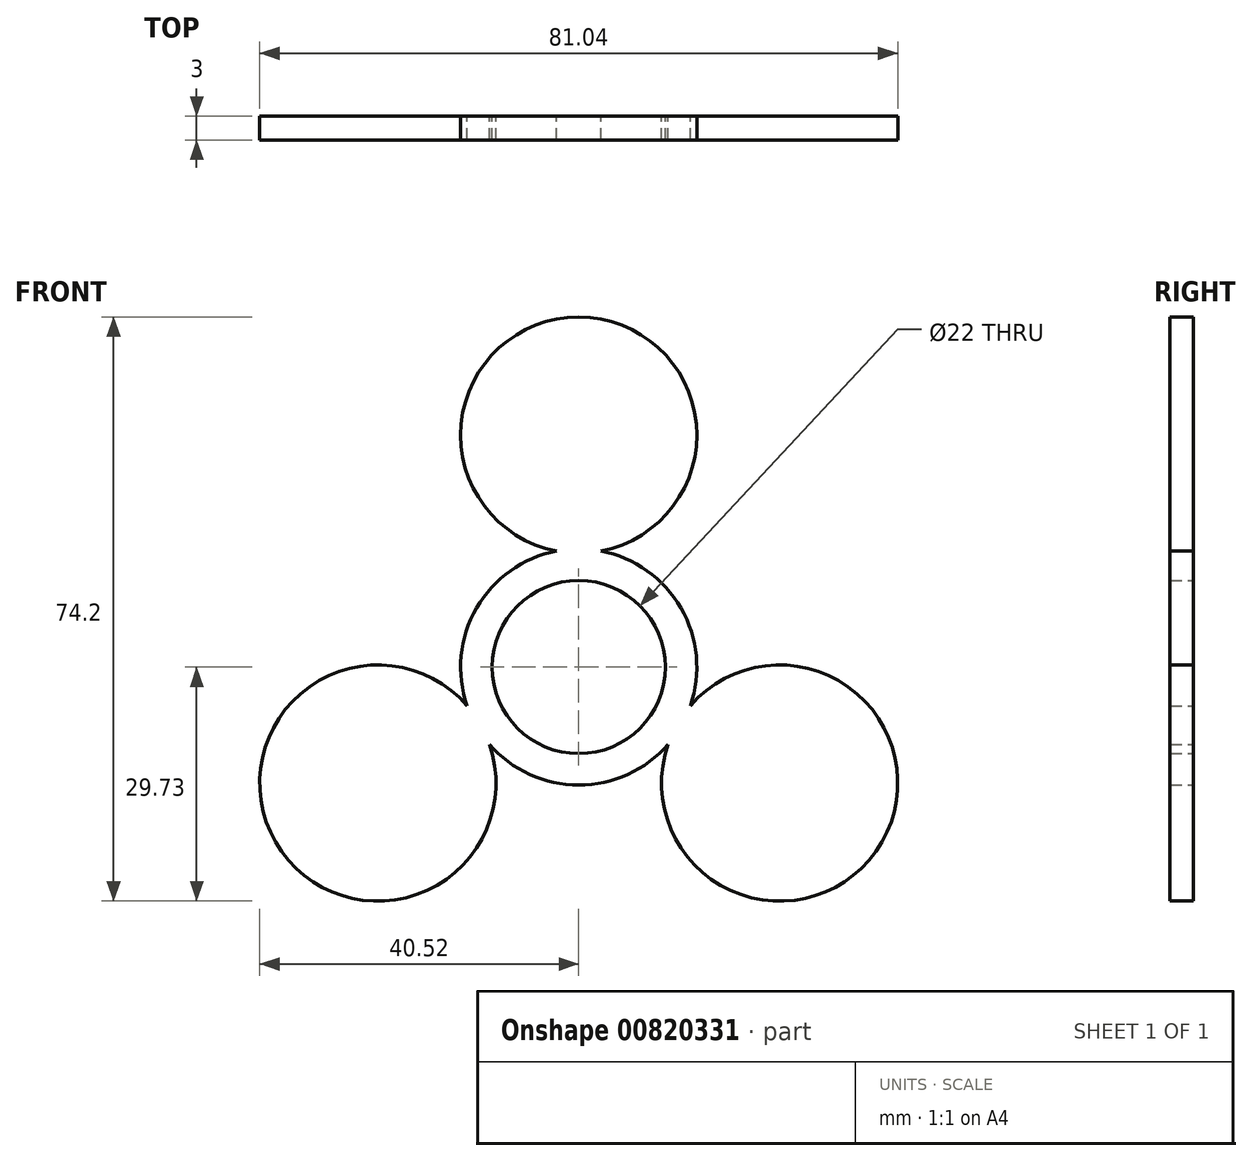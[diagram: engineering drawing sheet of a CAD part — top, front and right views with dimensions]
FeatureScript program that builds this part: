
annotation { "Feature Type Name" : "Feature", "Feature Type Description" : "" }
export const myFeature = defineFeature(function(context is Context, id is Id, definition is map)
    precondition{}
    {
        {
            var Q0;
            Q0=qCreatedBy(makeId("Front.planeOp"),FACE);
            var sketch = newSketch(context, id + "F0", { "sketchPlane" : qUnion([Q0])});
            skCircle(sketch, "E0", {"center": v(0, 0) * mm, "radius": 11 * mm});
            skArc(sketch, "E1", {"start": v(-2.8, 14.73) * mm, "mid": v(-13, 7.5) * mm, "end": v(-14.17, -4.93) * mm});
            skArc(sketch, "E2", {"start": v(2.8, 14.73) * mm, "mid": v(0, 44.47) * mm, "end": v(-2.8, 14.73) * mm});
            skArc(sketch, "E3.1.0", {"start": v(-14.17, -4.93) * mm, "mid": v(-38.51, -22.23) * mm, "end": v(-11.36, -9.8) * mm});
            skArc(sketch, "E3.2.0", {"start": v(11.36, -9.8) * mm, "mid": v(38.51, -22.23) * mm, "end": v(14.17, -4.93) * mm});
            skArc(sketch, "E4.trimOffspring", {"start": v(14.17, -4.93) * mm, "mid": v(13, 7.5) * mm, "end": v(2.8, 14.73) * mm});
            skArc(sketch, "E5.trimOffspring", {"start": v(-11.36, -9.8) * mm, "mid": v(0, -15) * mm, "end": v(11.36, -9.8) * mm});
            skSolve(sketch);
        }
        {
            var Q0;
            Q0=makeQuery(id+"F0.imprint","IMPRINT",FACE,{"disambiguationData":[TD([[makeQuery(id+"F0.imprint","IMPRINT",EDGE,{"derivedFrom":sQuery(id+"F0.wireOp",EDGE,"E0")}),-1.0]])]});
            extrude(context, id + "F1", {"entities" : qUnion([Q0]), "depth" : 3 * mm, "offsetDistance" : 25 * mm});
        }
    });
